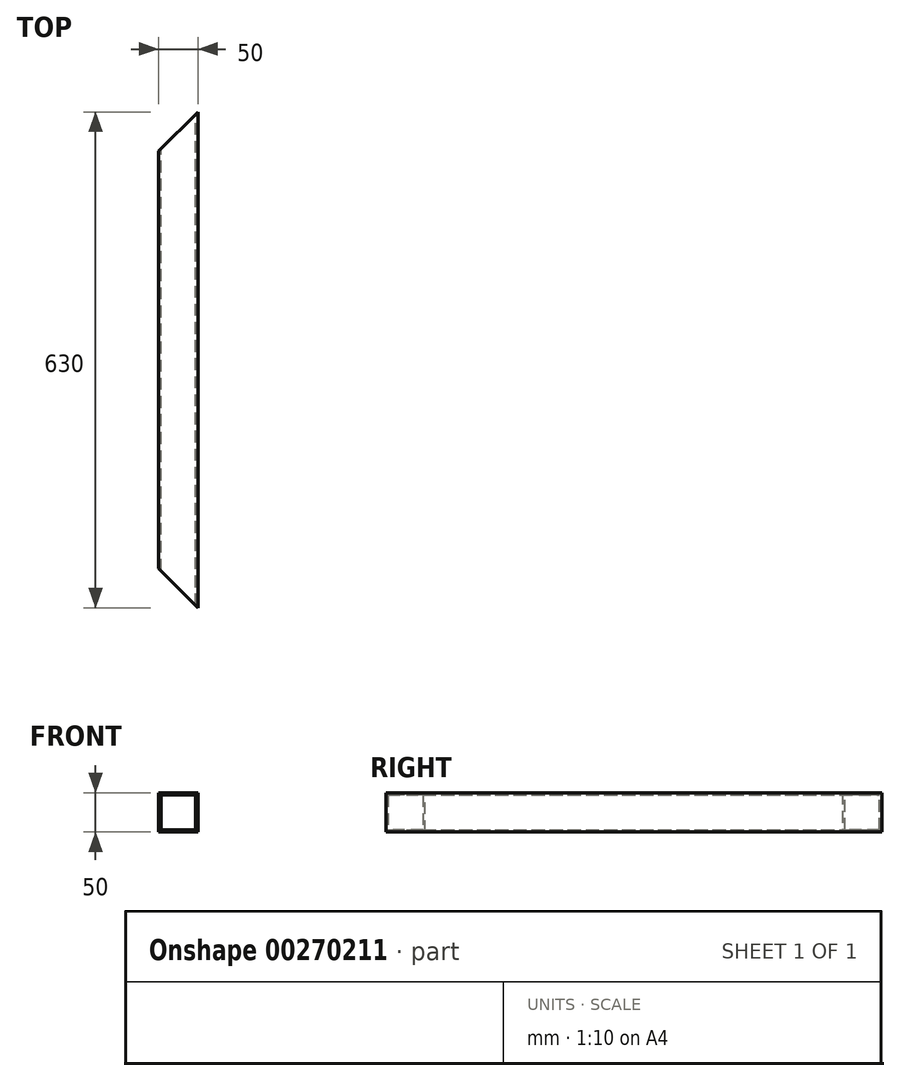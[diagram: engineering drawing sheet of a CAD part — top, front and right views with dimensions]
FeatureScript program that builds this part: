
annotation { "Feature Type Name" : "Feature", "Feature Type Description" : "" }
export const myFeature = defineFeature(function(context is Context, id is Id, definition is map)
    precondition{}
    {
        {
            var Q0;
            Q0=qCreatedBy(makeId("Front.planeOp"),FACE);
            var sketch = newSketch(context, id + "F0", { "sketchPlane" : qUnion([Q0])});
            skLineSegment(sketch, "E0.bottom", {"start": v(25, -25) * mm, "end": v(-25, -25) * mm});
            skLineSegment(sketch, "E0.top", {"start": v(25, 25) * mm, "end": v(-25, 25) * mm});
            skLineSegment(sketch, "E0.left", {"start": v(25, -25) * mm, "end": v(25, 25) * mm});
            skLineSegment(sketch, "E0.right", {"start": v(-25, -25) * mm, "end": v(-25, 25) * mm});
            skPoint(sketch, "E0.middle", {"position": v(0, 0) * mm});
            skLineSegment(sketch, "E1.bottom", {"start": v(22, -22) * mm, "end": v(-22, -22) * mm});
            skLineSegment(sketch, "E1.top", {"start": v(22, 22) * mm, "end": v(-22, 22) * mm});
            skLineSegment(sketch, "E1.left", {"start": v(22, -22) * mm, "end": v(22, 22) * mm});
            skLineSegment(sketch, "E1.right", {"start": v(-22, -22) * mm, "end": v(-22, 22) * mm});
            skSolve(sketch);
        }
        {
            var Q0;
            Q0=makeQuery(id+"F0.imprint","IMPRINT",FACE,{"disambiguationData":[TD([[makeQuery(id+"F0.imprint","IMPRINT",EDGE,{"derivedFrom":sQuery(id+"F0.wireOp",EDGE,"E0.bottom")}),-1.0]])]});
            extrude(context, id + "F1", {"entities" : qUnion([Q0]), "depth" : 630 * mm});
        }
        {
            var Q0;
            Q0=makeQuery(id+"F1.opExtrude","CAP_EDGE",EDGE,{"disambiguationData":[OSD([sQuery(id+"F0.wireOp",EDGE,"E0.right")])],"isStart":false});
            chamfer(context, id + "F2", {"entities" : qUnion([Q0]), "width" : 50 * mm, "tangentPropagation" : true});
        }
        {
            var Q0;
            Q0=makeQuery(id+"F1.opExtrude","CAP_EDGE",EDGE,{"disambiguationData":[OSD([sQuery(id+"F0.wireOp",EDGE,"E0.right")])],"isStart":true});
            chamfer(context, id + "F3", {"entities" : qUnion([Q0]), "width" : 50 * mm, "tangentPropagation" : true});
        }
    });
